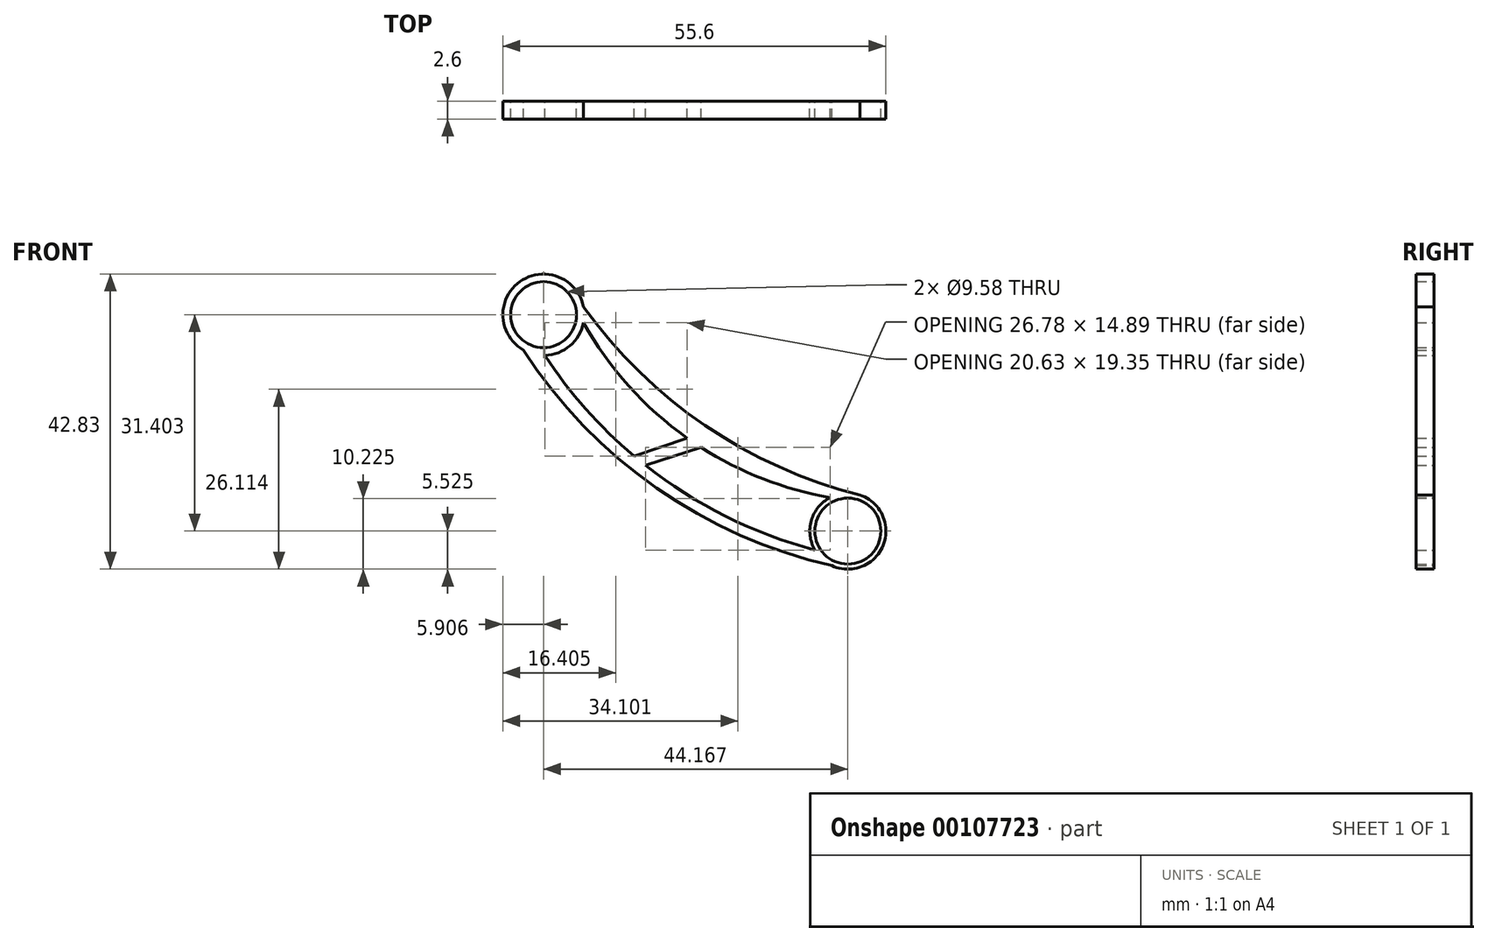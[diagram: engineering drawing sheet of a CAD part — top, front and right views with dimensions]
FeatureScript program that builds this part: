
annotation { "Feature Type Name" : "Feature", "Feature Type Description" : "" }
export const myFeature = defineFeature(function(context is Context, id is Id, definition is map)
    precondition{}
    {
        {
            var Q0;
            Q0=qCreatedBy(makeId("Front.planeOp"),FACE);
            var sketch = newSketch(context, id + "F0", { "sketchPlane" : qUnion([Q0])});
            skCircle(sketch, "E0", {"center": v(38.37, -32.54) * mm, "radius": 5.52 * mm});
            skArc(sketch, "E1", {"start": v(0, 0) * mm, "mid": v(17.64, -17.2) * mm, "end": v(40.1, -27.3) * mm});
            skArc(sketch, "E2", {"start": v(-8.73, -6.27) * mm, "mid": v(10.6, -26.29) * mm, "end": v(36.03, -37.55) * mm});
            skCircle(sketch, "E3", {"center": v(-5.8, -1.14) * mm, "radius": 5.9 * mm});
            skArc(sketch, "E4", {"start": v(0, -2.28) * mm, "mid": v(15.02, -19.03) * mm, "end": v(35.8, -27.66) * mm});
            skArc(sketch, "E5", {"start": v(-5.6, -7.04) * mm, "mid": v(11.37, -24.79) * mm, "end": v(33.58, -35.29) * mm});
            skPoint(sketch, "E6.endSnap0", {"position": v(15.02, -19.03) * mm});
            skLineSegment(sketch, "E7", {"start": v(9.01, -23) * mm, "end": v(17.06, -20.4) * mm});
            skLineSegment(sketch, "E8", {"start": v(7.33, -21.63) * mm, "end": v(15.02, -19.03) * mm});
            skSolve(sketch);
        }
        {
            var Q0;
            {var subQ0=sQuery(id+"F0.wireOp",EDGE,"E4");var subQ6=sQuery(id+"F0.wireOp",EDGE,"E0");var subQ8=makeQuery(id+"F0.imprint","INTERSECT",VERTEX,{"derivedFrom":[subQ6,subQ0]});Q0=makeQuery(id+"F0.imprint","IMPRINT",FACE,{"disambiguationData":[TD([[makeQuery(id+"F0.imprint","IMPRINT",EDGE,{"disambiguationData":[TD([[subQ8,1.0]])],"derivedFrom":subQ6}),-1.0]])]});}
            var Q1;
            {var subQ1=sQuery(id+"F0.wireOp",EDGE,"E0");var subQ5=makeQuery(id+"F0.imprint","INTERSECT",VERTEX,{"derivedFrom":[subQ1,sQuery(id+"F0.wireOp",EDGE,"E4")]});Q1=makeQuery(id+"F0.imprint","IMPRINT",FACE,{"disambiguationData":[TD([[makeQuery(id+"F0.imprint","IMPRINT",EDGE,{"disambiguationData":[TD([[subQ5,1.0]])],"derivedFrom":subQ1}),1.0]])]});}
            var Q2;
            {var subQ4=sQuery(id+"F0.wireOp",EDGE,"E2");Q2=makeQuery(id+"F0.imprint","IMPRINT",FACE,{"disambiguationData":[TD([[makeQuery(id+"F0.imprint","IMPRINT",EDGE,{"derivedFrom":subQ4}),1.0]])]});}
            var Q3;
            {var subQ0=sQuery(id+"F0.wireOp",EDGE,"E7");Q3=makeQuery(id+"F0.imprint","IMPRINT",FACE,{"disambiguationData":[TD([[makeQuery(id+"F0.imprint","IMPRINT",EDGE,{"derivedFrom":subQ0}),1.0]])]});}
            var Q4;
            {var subQ0=sQuery(id+"F0.wireOp",EDGE,"E3");var subQ1=makeQuery(id+"F0.imprint","INTERSECT",VERTEX,{"derivedFrom":[sQuery(id+"F0.wireOp",EDGE,"E1"),subQ0]});Q4=makeQuery(id+"F0.imprint","IMPRINT",FACE,{"disambiguationData":[TD([[makeQuery(id+"F0.imprint","IMPRINT",EDGE,{"disambiguationData":[TD([[subQ1,-1.0]])],"derivedFrom":subQ0}),1.0]])]});}
            extrude(context, id + "F1", {"entities" : qUnion([Q0, Q1, Q2, Q3, Q4]), "depth" : 2.6 * mm});
        }
        {
            var Q0;
            Q0=makeQuery(id+"F1.opExtrude","CAP_FACE",FACE,{"disambiguationData":[OSD([sQuery(id+"F0.wireOp",EDGE,"E0"),sQuery(id+"F0.wireOp",EDGE,"E1"),sQuery(id+"F0.wireOp",EDGE,"E2"),sQuery(id+"F0.wireOp",EDGE,"E3"),sQuery(id+"F0.wireOp",EDGE,"E4"),sQuery(id+"F0.wireOp",EDGE,"E5"),sQuery(id+"F0.wireOp",EDGE,"E7"),sQuery(id+"F0.wireOp",EDGE,"E8")])],"isStart":true});
            var sketch = newSketch(context, id + "F2", { "sketchPlane" : qUnion([Q0])});
            skCircle(sketch, "E9", {"center": v(5.8, -1.14) * mm, "radius": 4.79 * mm});
            skCircle(sketch, "E10", {"center": v(-38.37, -32.54) * mm, "radius": 4.79 * mm});
            skSolve(sketch);
        }
        {
            var Q0;
            Q0=makeQuery(id+"F2.imprint","IMPRINT",FACE,{"disambiguationData":[TD([[makeQuery(id+"F2.imprint","IMPRINT",EDGE,{"derivedFrom":sQuery(id+"F2.wireOp",EDGE,"E10")}),1.0]])]});
            var Q1;
            Q1=makeQuery(id+"F2.imprint","IMPRINT",FACE,{"disambiguationData":[TD([[makeQuery(id+"F2.imprint","IMPRINT",EDGE,{"derivedFrom":sQuery(id+"F2.wireOp",EDGE,"E9")}),1.0]])]});
            extrude(context, id + "F3", {"entities" : qUnion([Q0, Q1]), "operationType" : NewBodyOperationType.REMOVE, "oppositeDirection" : true, "depth" : 25.4 * mm});
        }
    });
